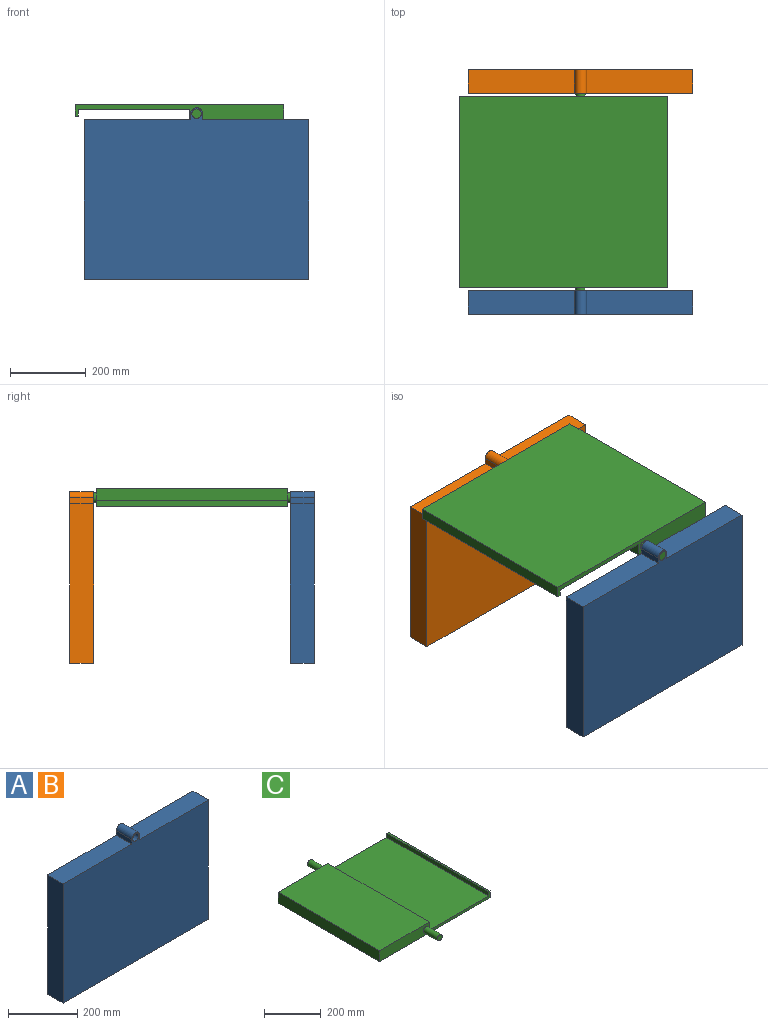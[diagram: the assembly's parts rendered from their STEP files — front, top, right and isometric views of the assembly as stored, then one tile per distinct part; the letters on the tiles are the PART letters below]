
ASSEMBLY  parts=3 mates=5
PART A: 11 faces, bbox 592x63x452 mm
  f0: plane 420x63mm, normal (1,0,0), area 26460mm2, adj f1,f8,f9,f10
  f1: plane 280x63mm, normal (0,0,1), area 17640mm2, adj f0,f2,f9,f10
  f2: plane 63x16mm, normal (1,0,0), area 1008mm2, adj f1,f3,f9,f10
  f3: cylinder r=16mm len=63mm, axis (0,1,0), area 3166.7mm2, adj f2,f4,f9,f10
  f4: plane 63x16mm, normal (-1,0,0), area 1008mm2, adj f3,f5,f9,f10
  f5: plane 280x63mm, normal (0,0,1), area 17640mm2, adj f4,f6,f9,f10
  f6: plane 420x63mm, normal (-1,0,0), area 26460mm2, adj f5,f8,f9,f10
  f7: cylinder r=12.5mm len=63mm, axis (0,1,0), area 4948mm2, adj f9,f10
  f8: plane 592x63mm, normal (0,0,-1), area 37296mm2, adj f0,f6,f9,f10
  f9: plane 592x452mm, normal (0,-1,0), area 249063.3mm2, adj f0,f1,f2,f3,f4,f5,f6,f7
  f10: plane 592x452mm, normal (0,1,0), area 249063.3mm2, adj f0,f1,f2,f3,f4,f5,f6,f7
PART B: same geometry as A
PART C: 14 faces, bbox 550x645x47 mm
  f0: plane 505x294mm, normal (0,0,1), area 148470mm2, adj f1,f3,f6,f8
  f1: plane 550x47mm, normal (0,-1,0), area 14933.1mm2, adj f0,f2,f4,f5,f6,f7,f8,f9
  f2: plane 505x30mm, normal (1,0,0), area 15150mm2, adj f1,f3,f5,f7
  f3: plane 550x47mm, normal (0,1,0), area 14933.1mm2, adj f0,f2,f4,f5,f6,f7,f8,f9
  f4: plane 505x47mm, normal (-1,0,0), area 23735mm2, adj f1,f3,f5,f9
  f5: plane 550x505mm, normal (0,0,-1), area 277750mm2, adj f1,f2,f3,f4
  f6: plane 505x18mm, normal (-1,0,0), area 9090mm2, adj f0,f1,f3,f7
  f7: plane 505x8mm, normal (0,0,1), area 4040mm2, adj f1,f2,f3,f6
  f8: plane 505x35mm, normal (1,0,0), area 17675mm2, adj f0,f1,f3,f9
  f9: plane 505x248mm, normal (0,0,1), area 125240mm2, adj f1,f3,f4,f8
  f10: cylinder r=12.5mm len=70mm, axis (0,1,0), area 5497.8mm2, adj f1,f11
  f11: plane 25x25mm, normal (0,-1,0), area 490.9mm2, adj f10
  f12: cylinder r=12.5mm len=70mm, axis (0,-1,0), area 5497.8mm2, adj f3,f13
  f13: plane 25x25mm, normal (0,1,0), area 490.9mm2, adj f12
PLACE A t=(483.52,265.34,128.97)mm fixed
PLACE B t=(483.52,847.34,128.97)mm
PLACE C rot(axis=(0,-1,0),180deg) t=(167.24,124.84,243.45)mm
MATE parallel A.f9 <-> B.f10  axis (0,-1,0) through (212.24,-197.66,-5.67)mm
MATE planar A.f1 <-> B.f1  axis (0,0,1) through (368.24,-166.16,203.95)mm
MATE planar A.f0 <-> B.f0  axis (1,0,0) through (508.24,-166.16,-6.05)mm
MATE revolute C.f10 <-> A.f3  axis (0,1,0) through (212.24,-197.66,219.95)mm
MATE revolute C.f10 <-> B.f3  axis (0,-1,0) through (212.24,447.34,219.95)mm
